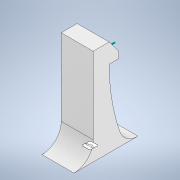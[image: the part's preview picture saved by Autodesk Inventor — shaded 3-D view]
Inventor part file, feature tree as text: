
AUTODESK INVENTOR PART (.ipt)
format: ipt  version: 2022 (Build 260153000, 153)  size: 153,088 bytes
history: native  units: mm
features: extrude x1, sketch x1
ambient origin geometry x8: Origin, YZ Plane, XZ Plane, XY Plane, X Axis, Y Axis, Z Axis, Center Point
bodies: Solid1 (feature_tree)
feature tree (2):
  extrude  "Extrusion1"  Depth=4.0mm
  sketch  "Sketch1"  dims[d0=12.0mm d1=4.0mm d2=1.5mm d3=3.0mm d4=2.5mm d5=1.0mm d6=5.0mm d7=0.0mm d15=3.0mm d17=3.0mm d18=3.0mm]
